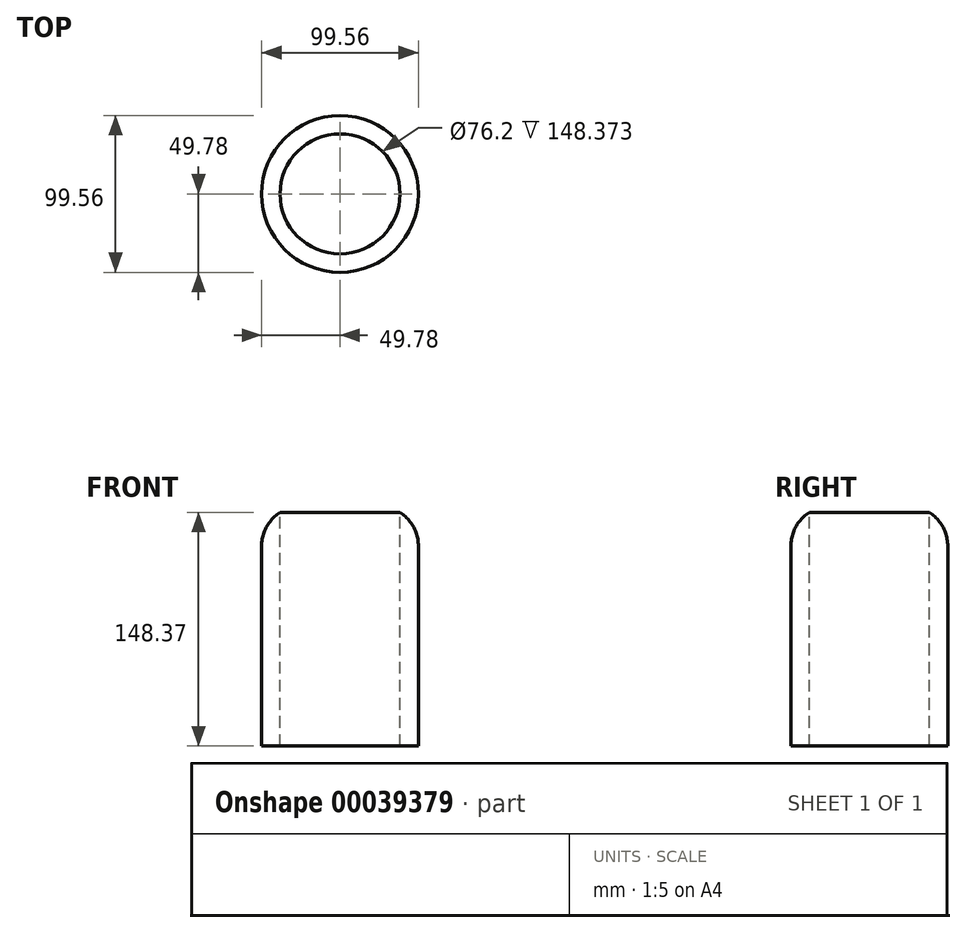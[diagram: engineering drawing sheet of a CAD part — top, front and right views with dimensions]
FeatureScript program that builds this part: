
annotation { "Feature Type Name" : "Feature", "Feature Type Description" : "" }
export const myFeature = defineFeature(function(context is Context, id is Id, definition is map)
    precondition{}
    {
        {
            var Q0;
            Q0=qCreatedBy(makeId("Top.planeOp"),FACE);
            var sketch = newSketch(context, id + "F0", { "sketchPlane" : qUnion([Q0])});
            skCircle(sketch, "E0", {"center": v(0, 0) * mm, "radius": 49.78 * mm});
            skSolve(sketch);
        }
        {
            var Q0;
            Q0 = qSketchRegion(id + "F0", true);
            extrude(context, id + "F1", {"entities" : qUnion([Q0]), "depth" : 152.4 * mm});
        }
        {
            var Q0;
            Q0=makeQuery(id+"F1.opExtrude","CAP_EDGE",EDGE,{"disambiguationData":[OSD([sQuery(id+"F0.wireOp",EDGE,"E0")])],"isStart":false});
            fillet(context, id + "F2", {"entities" : qUnion([Q0]), "radius" : 25.4 * mm, "tangentPropagation" : true, "allowEdgeOverflow" : false});
        }
        {
            var Q0;
            Q0=makeQuery(id+"F1.opExtrude","CAP_FACE",FACE,{"disambiguationData":[OSD([sQuery(id+"F0.wireOp",EDGE,"E0")])],"isStart":false});
            var sketch = newSketch(context, id + "F3", { "sketchPlane" : qUnion([Q0])});
            skCircle(sketch, "E1", {"center": v(0, 0) * mm, "radius": 9.32 * mm});
            skSolve(sketch);
        }
        {
            var Q0;
            Q0=sQuery(id+"F3.wireOp",VERTEX,"E1.center");
            var Q1;
            Q1=makeQuery(id+"F1.opExtrude","SWEPT_BODY",BODY,{"disambiguationData":[OSD([sQuery(id+"F0.wireOp",EDGE,"E0")])]});
            hole(context, id + "F4", {"style" : HoleStyle.SIMPLE, "holeDiameter" : 76.2 * mm, "endStyle" : HoleEndStyle.THROUGH, "locations" : qUnion([Q0]), "scope" : qUnion([Q1])});
        }
        {
            var Q0;
            Q0=qCreatedBy(makeId("Right.planeOp"),FACE);
            var sketch = newSketch(context, id + "F5", { "sketchPlane" : qUnion([Q0])});
            skCircle(sketch, "E2", {"center": v(-182.78, 201.94) * mm, "radius": 21.86 * mm});
            skSolve(sketch);
        }
        {
            var Q0;
            Q0=sQuery(id+"F5.wireOp",EDGE,"E2");
            extrude(context, id + "F6", {"bodyType" : ToolBodyType.SURFACE, "surfaceEntities" : qUnion([Q0]), "depth" : 254 * mm});
        }
    });
